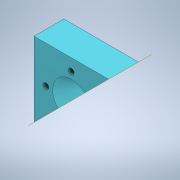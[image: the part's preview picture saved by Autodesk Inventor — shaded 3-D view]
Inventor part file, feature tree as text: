
AUTODESK INVENTOR PART (.ipt)
format: ipt  version: 2022.1 (Build 261234000, 234)  size: 990,720 bytes
history: native  units: mm
features: sketch x7, extrude x2, revolve x2, emboss x2, hole x1, plane x1, split x1
ambient origin geometry x8: Origin, YZ Plane, XZ Plane, XY Plane, X Axis, Y Axis, Z Axis, Center Point
bodies: Solid7 (feature_tree)
feature tree (16):
  extrude  "Extrusion20"  Depth=50.0mm
  revolve  "Revolution4"  [1 undecoded]
  extrude  "Extrusion21"  TaperAngle=90.0deg  [1 undecoded]
  revolve  "Revolution5"  [1 undecoded]
  hole  "Hole2"  [1 undecoded]
  plane  "Work Plane6"
  emboss  "Emboss3"
  emboss  "Emboss4"
  split  "Split1"
  sketch  "Sketch27"  dims[d124=50.0mm d125=50.0mm]
  sketch  "Sketch28"  dims[d126=15.0mm d127=0.0mm d128=3.0mm]
  sketch  "Sketch29"  dims[d129=12.5mm d130=90.0deg]
  sketch  "Sketch30"  dims[d131=5.0mm d132=0.0mm d133=2.5mm]
  sketch  "Sketch31"  dims[d134=90.0deg d135=34.0mm]
  sketch  "Sketch32"  dims[d136=34.0mm]
  sketch  "Sketch33"  dims[d137=3.81mm d138=6.0mm d139=8.89mm d140=3.145mm d141=14.3117mm d142=8.0mm d143=20.594885mm d144=1.0mm d145=0.0mm d146=1.0mm d147=0.0mm]
note: 4 required parameter values undecoded (feature->parameter linkage not recoverable at this tier; creation-order binding heuristic only, values carry confidence <= 0.55)